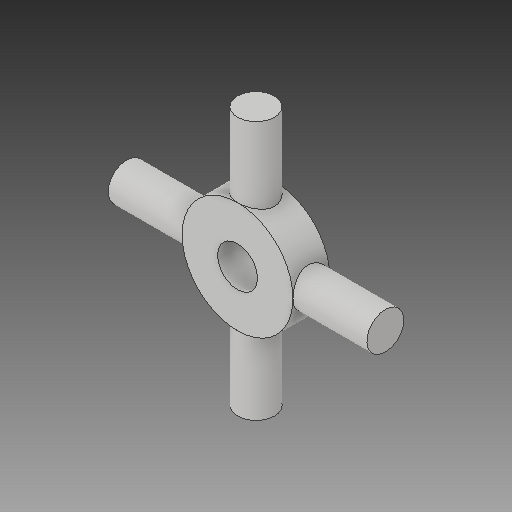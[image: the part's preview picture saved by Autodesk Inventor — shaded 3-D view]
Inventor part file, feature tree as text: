
AUTODESK INVENTOR PART (.ipt)
format: ipt  version: 2019 (Build 230136000, 136)  size: 137,216 bytes
history: native  units: in
note: dims shown in document units (in); Inventor stores cm internally (conversion verified against a paired STEP export)
features: sketch x5, extrude x2, pattern_circular x1, hole x1, plane x1
ambient origin geometry x8: Origin, YZ Plane, XZ Plane, XY Plane, X Axis, Y Axis, Z Axis, Center Point
bodies: Solid1 (feature_tree)
feature tree (10):
  extrude  "Extrusion1"  Depth=0.25in TaperAngle=0.0deg
  pattern_circular  "Circular Pattern1"  Count=4 Angle=360.0deg
  extrude  "Extrusion2"  Depth=0.25in TaperAngle=0.0deg
  hole  "Hole1"  [1 undecoded]
  sketch  "Sketch4"
  plane  "Work Plane1"
  sketch  "Sketch5"
  sketch  "Sketch1"  dims[d0=0.25in d1=0.875in d2=0.0in d3=1.5748in d4=360.0deg]
  sketch  "Sketch2"  dims[d6=0.75in d7=0.25in d8=0.0in]
  sketch  "Sketch3"  dims[d9=0.27in d10=0.75in d11=0.375in d12=0.25in d13=0.5635in d14=1.0in d15=0.8108in d16=45.0deg]
note: 1 required parameter value undecoded (feature->parameter linkage not recoverable at this tier; creation-order binding heuristic only, values carry confidence <= 0.55)
